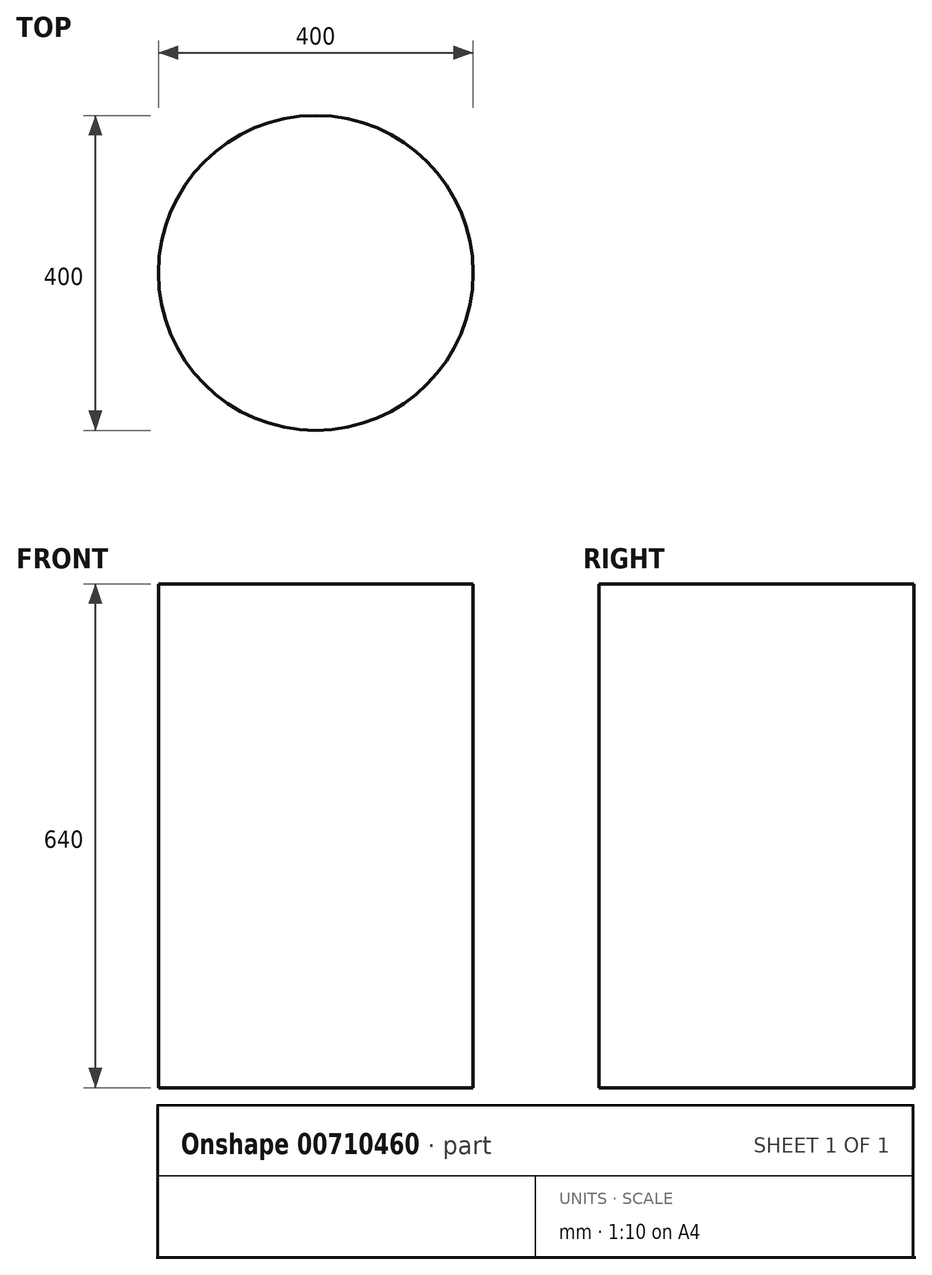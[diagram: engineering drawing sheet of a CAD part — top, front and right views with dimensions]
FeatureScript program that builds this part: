
annotation { "Feature Type Name" : "Feature", "Feature Type Description" : "" }
export const myFeature = defineFeature(function(context is Context, id is Id, definition is map)
    precondition{}
    {
        {
            var Q0;
            Q0=qCreatedBy(makeId("Top.planeOp"),FACE);
            var sketch = newSketch(context, id + "F0", { "sketchPlane" : qUnion([Q0])});
            skCircle(sketch, "E0", {"center": v(0, 0) * mm, "radius": 200 * mm});
            skSolve(sketch);
        }
        {
            var Q0;
            Q0=makeQuery(id+"F0.imprint","IMPRINT",FACE,{"disambiguationData":[TD([[makeQuery(id+"F0.imprint","IMPRINT",EDGE,{"derivedFrom":sQuery(id+"F0.wireOp",EDGE,"E0")}),1.0]])]});
            extrude(context, id + "F1", {"entities" : qUnion([Q0]), "depth" : 640 * mm, "offsetDistance" : 25 * mm});
        }
    });
